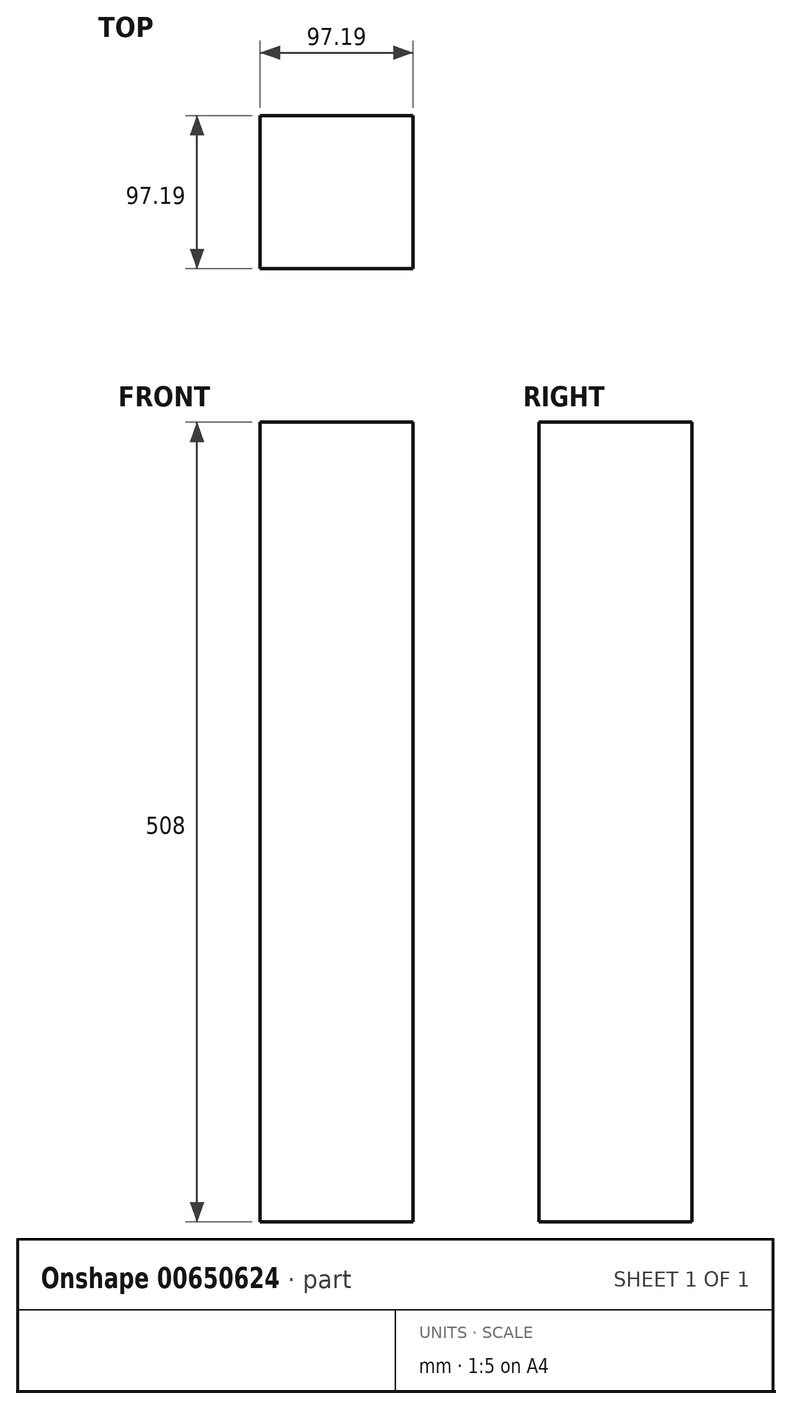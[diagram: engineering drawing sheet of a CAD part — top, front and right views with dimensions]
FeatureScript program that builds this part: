
annotation { "Feature Type Name" : "Feature", "Feature Type Description" : "" }
export const myFeature = defineFeature(function(context is Context, id is Id, definition is map)
    precondition{}
    {
        {
            var Q0;
            Q0=qCreatedBy(makeId("Top.planeOp"),FACE);
            var sketch = newSketch(context, id + "F0", { "sketchPlane" : qUnion([Q0])});
            skLineSegment(sketch, "E0.bottom", {"start": v(-41.6, 41.98) * mm, "end": v(55.59, 41.98) * mm});
            skLineSegment(sketch, "E0.top", {"start": v(-41.6, -55.2) * mm, "end": v(55.59, -55.2) * mm});
            skLineSegment(sketch, "E0.left", {"start": v(-41.6, 41.98) * mm, "end": v(-41.6, -55.2) * mm});
            skLineSegment(sketch, "E0.right", {"start": v(55.59, 41.98) * mm, "end": v(55.59, -55.2) * mm});
            skSolve(sketch);
        }
        {
            var Q0;
            Q0 = qSketchRegion(id + "F0", true);
            extrude(context, id + "F1", {"entities" : qUnion([Q0]), "depth" : 508 * mm, "offsetDistance" : 25.4 * mm});
        }
    });
